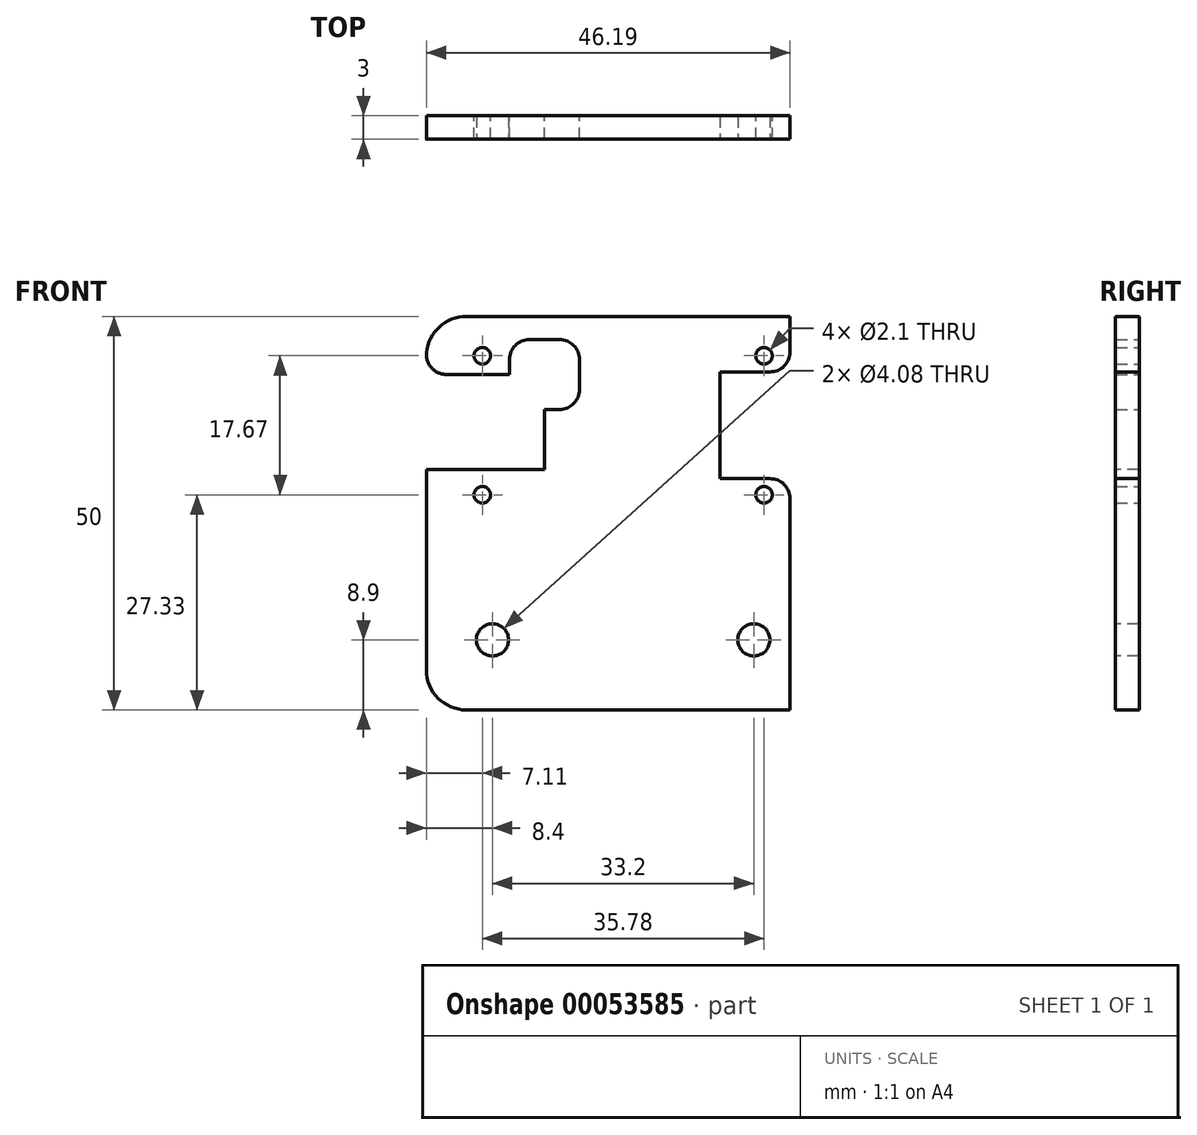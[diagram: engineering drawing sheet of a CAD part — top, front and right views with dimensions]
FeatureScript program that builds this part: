
annotation { "Feature Type Name" : "Feature", "Feature Type Description" : "" }
export const myFeature = defineFeature(function(context is Context, id is Id, definition is map)
    precondition{}
    {
        {
            var Q0;
            Q0=qCreatedBy(makeId("Front.planeOp"),FACE);
            var sketch = newSketch(context, id + "F0", { "sketchPlane" : qUnion([Q0])});
            skLineSegment(sketch, "E0.bottom", {"start": v(0, 0) * mm, "end": v(50, 0) * mm});
            skLineSegment(sketch, "E0.top", {"start": v(0, 50) * mm, "end": v(50, 50) * mm});
            skLineSegment(sketch, "E0.left", {"start": v(0, 0) * mm, "end": v(0, 50) * mm});
            skLineSegment(sketch, "E0.right", {"start": v(50, 0) * mm, "end": v(50, 50) * mm});
            skCircle(sketch, "E1", {"center": v(7.11, 45) * mm, "radius": 1.05 * mm});
            skCircle(sketch, "E2", {"center": v(7.11, 27.33) * mm, "radius": 1.05 * mm});
            skCircle(sketch, "E3", {"center": v(42.9, 27.33) * mm, "radius": 1.05 * mm});
            skCircle(sketch, "E4", {"center": v(42.9, 45) * mm, "radius": 1.05 * mm});
            skLineSegment(sketch, "E5", {"start": v(0, 45) * mm, "end": v(7.11, 45) * mm, "construction": true});
            skLineSegment(sketch, "E6", {"start": v(42.9, 45) * mm, "end": v(50, 45) * mm, "construction": true});
            skLineSegment(sketch, "E7", {"start": v(7.11, 45) * mm, "end": v(7.11, 50) * mm, "construction": true});
            skSolve(sketch);
        }
        {
            var Q0;
            Q0 = qSketchRegion(id + "F0", true);
            extrude(context, id + "F1", {"entities" : qUnion([Q0]), "depth" : 3 * mm});
        }
        {
            var Q0;
            Q0=makeQuery(id+"F1.opExtrude","CAP_FACE",FACE,{"disambiguationData":[OSD([sQuery(id+"F0.wireOp",EDGE,"E0.bottom"),sQuery(id+"F0.wireOp",EDGE,"E0.top"),sQuery(id+"F0.wireOp",EDGE,"E0.left"),sQuery(id+"F0.wireOp",EDGE,"E0.right"),sQuery(id+"F0.wireOp",EDGE,"E1"),sQuery(id+"F0.wireOp",EDGE,"E2"),sQuery(id+"F0.wireOp",EDGE,"E3"),sQuery(id+"F0.wireOp",EDGE,"E4")])],"isStart":false});
            var sketch = newSketch(context, id + "F2", { "sketchPlane" : qUnion([Q0])});
            skLineSegment(sketch, "E8.bottom", {"start": v(0, 42.62) * mm, "end": v(15, 42.62) * mm});
            skLineSegment(sketch, "E8.top", {"start": v(0, 30.53) * mm, "end": v(15, 30.53) * mm});
            skLineSegment(sketch, "E8.left", {"start": v(0, 42.62) * mm, "end": v(0, 30.53) * mm});
            skLineSegment(sketch, "E8.right", {"start": v(15, 42.62) * mm, "end": v(15, 30.53) * mm});
            skLineSegment(sketch, "E9", {"start": v(7.11, 26.28) * mm, "end": v(-16.3, 26.28) * mm, "construction": true});
            skSolve(sketch);
        }
        {
            var Q0;
            Q0=makeQuery(id+"F2.imprint","IMPRINT",FACE,{"disambiguationData":[TD([[makeQuery(id+"F2.imprint","IMPRINT",EDGE,{"derivedFrom":sQuery(id+"F2.wireOp",EDGE,"E8.bottom")}),-1.0]])]});
            extrude(context, id + "F3", {"entities" : qUnion([Q0]), "operationType" : NewBodyOperationType.REMOVE, "endBound" : BoundingType.THROUGH_ALL, "oppositeDirection" : true, "depth" : 25.4 * mm});
        }
        {
            var Q0;
            Q0=makeQuery(id+"F1.opExtrude","CAP_FACE",FACE,{"disambiguationData":[OSD([sQuery(id+"F0.wireOp",EDGE,"E0.bottom"),sQuery(id+"F0.wireOp",EDGE,"E0.top"),sQuery(id+"F0.wireOp",EDGE,"E0.left"),sQuery(id+"F0.wireOp",EDGE,"E0.right"),sQuery(id+"F0.wireOp",EDGE,"E1"),sQuery(id+"F0.wireOp",EDGE,"E2"),sQuery(id+"F0.wireOp",EDGE,"E3"),sQuery(id+"F0.wireOp",EDGE,"E4")])],"isStart":false});
            var sketch = newSketch(context, id + "F4", { "sketchPlane" : qUnion([Q0])});
            skCircle(sketch, "E10", {"center": v(8.4, 8.9) * mm, "radius": 2.04 * mm});
            skCircle(sketch, "E11", {"center": v(41.6, 8.9) * mm, "radius": 2.04 * mm});
            skLineSegment(sketch, "E12", {"start": v(8.4, 8.9) * mm, "end": v(0, 8.9) * mm, "construction": true});
            skLineSegment(sketch, "E13", {"start": v(41.6, 8.9) * mm, "end": v(50, 8.9) * mm, "construction": true});
            skSolve(sketch);
        }
        {
            var Q0;
            Q0 = qSketchRegion(id + "F4", true);
            extrude(context, id + "F5", {"entities" : qUnion([Q0]), "operationType" : NewBodyOperationType.REMOVE, "endBound" : BoundingType.THROUGH_ALL, "oppositeDirection" : true, "depth" : 25.4 * mm});
        }
        {
            var Q0;
            Q0=makeQuery(id+"F1.opExtrude","CAP_FACE",FACE,{"disambiguationData":[OSD([sQuery(id+"F0.wireOp",EDGE,"E0.bottom"),sQuery(id+"F0.wireOp",EDGE,"E0.top"),sQuery(id+"F0.wireOp",EDGE,"E0.left"),sQuery(id+"F0.wireOp",EDGE,"E0.right"),sQuery(id+"F0.wireOp",EDGE,"E1"),sQuery(id+"F0.wireOp",EDGE,"E2"),sQuery(id+"F0.wireOp",EDGE,"E3"),sQuery(id+"F0.wireOp",EDGE,"E4")])],"isStart":false});
            var sketch = newSketch(context, id + "F6", { "sketchPlane" : qUnion([Q0])});
            skLineSegment(sketch, "E14.bottom", {"start": v(46.2, 29.38) * mm, "end": v(37.3, 29.38) * mm});
            skLineSegment(sketch, "E14.top", {"start": v(46.2, 42.95) * mm, "end": v(37.3, 42.95) * mm});
            skLineSegment(sketch, "E14.left", {"start": v(50, 29.38) * mm, "end": v(50, 42.95) * mm});
            skLineSegment(sketch, "E14.right", {"start": v(37.3, 29.38) * mm, "end": v(37.3, 42.95) * mm});
            skLineSegment(sketch, "E15", {"start": v(42.9, 28.38) * mm, "end": v(33.59, 28.38) * mm, "construction": true});
            skLineSegment(sketch, "E16", {"start": v(42.9, 43.95) * mm, "end": v(29.78, 43.95) * mm, "construction": true});
            skLineSegment(sketch, "E17", {"start": v(46.2, 50) * mm, "end": v(46.2, 42.95) * mm});
            skLineSegment(sketch, "E18", {"start": v(46.2, 29.38) * mm, "end": v(46.2, 0) * mm});
            skLineSegment(sketch, "E19", {"start": v(50, 0) * mm, "end": v(50, 50) * mm});
            skLineSegment(sketch, "E20", {"start": v(50, 50) * mm, "end": v(46.2, 50) * mm});
            skLineSegment(sketch, "E21", {"start": v(50, 0) * mm, "end": v(46.2, 0) * mm});
            skSolve(sketch);
        }
        {
            var Q0;
            Q0 = qSketchRegion(id + "F6", true);
            extrude(context, id + "F7", {"entities" : qUnion([Q0]), "operationType" : NewBodyOperationType.REMOVE, "endBound" : BoundingType.THROUGH_ALL, "oppositeDirection" : true, "depth" : 25.4 * mm});
        }
        {
            var Q0;
            Q0=makeQuery(id+"F1.opExtrude","CAP_FACE",FACE,{"disambiguationData":[OSD([sQuery(id+"F0.wireOp",EDGE,"E0.bottom"),sQuery(id+"F0.wireOp",EDGE,"E0.top"),sQuery(id+"F0.wireOp",EDGE,"E0.left"),sQuery(id+"F0.wireOp",EDGE,"E0.right"),sQuery(id+"F0.wireOp",EDGE,"E1"),sQuery(id+"F0.wireOp",EDGE,"E2"),sQuery(id+"F0.wireOp",EDGE,"E3"),sQuery(id+"F0.wireOp",EDGE,"E4")])],"isStart":true});
            var sketch = newSketch(context, id + "F8", { "sketchPlane" : qUnion([Q0])});
            skLineSegment(sketch, "E22.rect.bottom", {"start": v(-10.55, 38.17) * mm, "end": v(-19.45, 38.17) * mm});
            skLineSegment(sketch, "E22.rect.top", {"start": v(-10.55, 47.07) * mm, "end": v(-19.45, 47.07) * mm});
            skLineSegment(sketch, "E22.rect.left", {"start": v(-10.55, 38.17) * mm, "end": v(-10.55, 47.07) * mm});
            skLineSegment(sketch, "E22.rect.right", {"start": v(-19.45, 38.17) * mm, "end": v(-19.45, 47.07) * mm});
            skPoint(sketch, "E22.rect.middle", {"position": v(-15, 42.62) * mm});
            skSolve(sketch);
        }
        {
            var Q0;
            Q0 = qSketchRegion(id + "F8", true);
            extrude(context, id + "F9", {"entities" : qUnion([Q0]), "operationType" : NewBodyOperationType.REMOVE, "endBound" : BoundingType.THROUGH_ALL, "oppositeDirection" : true, "depth" : 25.4 * mm});
        }
        {
            var Q0;
            Q0=makeQuery(id+"F1.opExtrude","SWEPT_EDGE",EDGE,{"disambiguationData":[OSD([sQuery(id+"F0.wireOp",EDGE,"E0.top"),sQuery(id+"F0.wireOp",EDGE,"E0.left")])]});
            var Q1;
            Q1=makeQuery(id+"F1.opExtrude","SWEPT_EDGE",EDGE,{"disambiguationData":[OSD([sQuery(id+"F0.wireOp",EDGE,"E0.bottom"),sQuery(id+"F0.wireOp",EDGE,"E0.left")])]});
            var Q2;
            Q2=makeQuery(id+"F1.opExtrude","SWEPT_EDGE",EDGE,{"disambiguationData":[OSD([sQuery(id+"F0.wireOp",EDGE,"E0.bottom"),sQuery(id+"F0.wireOp",EDGE,"E0.right")])]});
            var Q3;
            Q3=makeQuery(id+"F1.opExtrude","SWEPT_EDGE",EDGE,{"disambiguationData":[OSD([sQuery(id+"F0.wireOp",EDGE,"E0.top"),sQuery(id+"F0.wireOp",EDGE,"E0.right")])]});
            fillet(context, id + "F10", {"entities" : qUnion([Q0, Q1, Q2, Q3]), "radius" : 5.08 * mm, "tangentPropagation" : true, "allowEdgeOverflow" : false});
        }
        {
            var Q0;
            Q0=makeQuery(id+"F9.boolean.opBoolean","COPY",EDGE,{"derivedFrom":makeQuery(id+"F9.opExtrude","SWEPT_EDGE",EDGE,{"disambiguationData":[OSD([sQuery(id+"F8.wireOp",EDGE,"E22.rect.top"),sQuery(id+"F8.wireOp",EDGE,"E22.rect.right")])]})});
            var Q1;
            Q1=makeQuery(id+"F9.boolean.opBoolean","COPY",EDGE,{"derivedFrom":makeQuery(id+"F9.opExtrude","SWEPT_EDGE",EDGE,{"disambiguationData":[OSD([sQuery(id+"F8.wireOp",EDGE,"E22.rect.bottom"),sQuery(id+"F8.wireOp",EDGE,"E22.rect.right")])]})});
            var Q2;
            Q2=makeQuery(id+"F9.boolean.opBoolean","COPY",EDGE,{"derivedFrom":makeQuery(id+"F9.opExtrude","SWEPT_EDGE",EDGE,{"disambiguationData":[OSD([sQuery(id+"F8.wireOp",EDGE,"E22.rect.top"),sQuery(id+"F8.wireOp",EDGE,"E22.rect.left")])]})});
            fillet(context, id + "F11", {"entities" : qUnion([Q0, Q1, Q2]), "radius" : 2.54 * mm, "tangentPropagation" : true, "allowEdgeOverflow" : false});
        }
        {
            var Q0;
            Q0=makeQuery(id+"F7.boolean.opBoolean","COPY",EDGE,{"derivedFrom":makeQuery(id+"F7.opExtrude","SWEPT_EDGE",EDGE,{"disambiguationData":[OSD([sQuery(id+"F0.wireOp",EDGE,"E0.top"),sQuery(id+"F6.wireOp",EDGE,"E17"),sQuery(id+"F6.wireOp",EDGE,"E20")])]})});
            var Q1;
            Q1=makeQuery(id+"F7.boolean.opBoolean","COPY",EDGE,{"derivedFrom":makeQuery(id+"F7.opExtrude","SWEPT_EDGE",EDGE,{"disambiguationData":[OSD([sQuery(id+"F6.wireOp",EDGE,"E14.bottom"),sQuery(id+"F6.wireOp",EDGE,"E18")])]})});
            var Q2;
            Q2=makeQuery(id+"F7.boolean.opBoolean","COPY",EDGE,{"derivedFrom":makeQuery(id+"F7.opExtrude","SWEPT_EDGE",EDGE,{"disambiguationData":[OSD([sQuery(id+"F0.wireOp",EDGE,"E0.right"),sQuery(id+"F6.wireOp",EDGE,"d59521cb-e5f2-46d7-bd4d-6c651d4cf2fd"),sQuery(id+"F6.wireOp",EDGE,"E19")])]})});
            var Q3;
            Q3=makeQuery(id+"F7.boolean.opBoolean","COPY",EDGE,{"derivedFrom":makeQuery(id+"F7.opExtrude","SWEPT_EDGE",EDGE,{"disambiguationData":[OSD([sQuery(id+"F6.wireOp",EDGE,"E14.top"),sQuery(id+"F6.wireOp",EDGE,"E17")])]})});
            var Q4;
            Q4=makeQuery(id+"F3.boolean.opBoolean","COPY",EDGE,{"derivedFrom":makeQuery(id+"F3.opExtrude","SWEPT_EDGE",EDGE,{"disambiguationData":[OSD([sQuery(id+"F0.wireOp",EDGE,"E0.left"),sQuery(id+"F2.wireOp",EDGE,"E8.bottom"),sQuery(id+"F2.wireOp",EDGE,"E8.left")])]})});
            var Q5;
            Q5=makeQuery(id+"F3.boolean.opBoolean","COPY",EDGE,{"derivedFrom":makeQuery(id+"F3.opExtrude","SWEPT_EDGE",EDGE,{"disambiguationData":[OSD([sQuery(id+"F0.wireOp",EDGE,"E0.left"),sQuery(id+"F2.wireOp",EDGE,"E8.top"),sQuery(id+"F2.wireOp",EDGE,"E8.left")])]})});
            var Q6;
            Q6=makeQuery(id+"F7.boolean.opBoolean","COPY",EDGE,{"derivedFrom":makeQuery(id+"F7.opExtrude","SWEPT_EDGE",EDGE,{"disambiguationData":[OSD([sQuery(id+"F0.wireOp",EDGE,"E0.bottom"),sQuery(id+"F6.wireOp",EDGE,"E18"),sQuery(id+"F6.wireOp",EDGE,"E21")])]})});
            fillet(context, id + "F12", {"entities" : qUnion([Q0, Q1, Q2, Q3, Q4, Q5, Q6]), "radius" : 2.54 * mm, "tangentPropagation" : true, "allowEdgeOverflow" : false});
        }
    });
